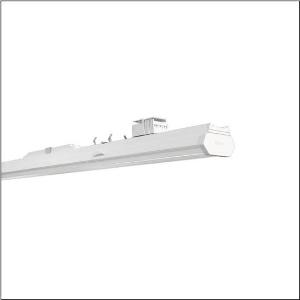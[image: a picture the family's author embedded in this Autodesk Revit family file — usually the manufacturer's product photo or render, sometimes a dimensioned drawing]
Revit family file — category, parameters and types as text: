
# Revit family: licross_r__11_protected_ho_51tp12dn4fxm3s4_aaf8
name_source: partatom
category: Lighting Fixtures
units: mm (PartAtom-declared; Revit-internal decimal feet)

## family parameters
Cut with Voids When Loaded = No
Host = Face
Light Source = No
Part Type = Normal
Room Calculation Point = No
Round Connector Dimension = Use Diameter
Shared = No

## types (1)
- --- (1 x LED, 970 lm, 7.4 W, 4000K)
    Apparent Load = 7 VA
    CIE Flux Codes = 70 91 97 98 100
    Color Rendering = 80
    Color Temperature = 4000K
    Default Elevation = 1800 mm
    Description = Licross® 11 Protected HO, luminaire insert, of sheet steel, galvanised, coil coated, white, length: 1.500mm, width: 90mm, height: 101mm, LED rated luminous flux: 15.270lm, light colour: 840, control gear: DALI 2, with plug, 6-pole, with phase selection, for trunking rail, 9 or 11-core, mains connection: 220..240V, AC, 50/60Hz, rated input power: 91W, for trunking rail, 9-/11-core, halogen-free wiring, for emergency light function, converter,control gear: single battery element, battery: LiFePO4, 9Ah, primary light control with lens, of plastic, primary optical cover: cover, of PMMA, light emission: direct distribution, primary light characteristic: symmetric, protection rating (complete): IP64, insulation class (complete): insulation class I (protective earthing), certification: CE, UKCA, protection symbol: D if used in an environment with conductive dust loads with corresponding accessories, impact resistance: IK06, permissible ambient temperature for indoor applications: +5..+30°C, standard: EN 60598-2-22, LABS conformity tested according to VDMA 24364:2018-05, reducing of maximum allowable ambient temperature of 5°C with ceiling mounting, corresponds to IFS (International Featured Standards) requirements for safety and quality in the food industry, packaging unit: 1 piece
    Height = 92 mm
    Lamp = 1 x LED
    Lamp Light Flux = 970 lm
    Lamp Power = 7.4 W
    Lamp count = 1
    Length = 1500 mm
    Luminous efficacy = 131 lm/W
    Manufacturer = Siteco
    ModVariant = No
    Model = 51TP12DN4FXM3S4
    Mounting Place = Ceiling
    Mounting Type = Pendant
    Number of Poles = 1
    OnlyDefault = Yes
    Power Factor = 1
    Product Name = Licross® 11 Protected HO
    Product group = luminaire insert
    ProductGroupID = 901
    Protection Class = Protection class I
    Protection Degree = IP 64
    RLX_Detail_Level = 1
    RLX_Emergency_Light_Flux = 0 lm
    RLX_Emergency_Type = 0
    RLX_Emergency_Type_DB = No
    RlxData = <blob elided: 24793 chars, md5=59a09943>
    Socket = socket
    Standby Power = 0 W
    System Light Flux = 970 lm
    System Power = 7 W
    Type Comments = : emergency light operation: 3 h
    Type Image = l_1256148.jpg
    URL = http://relux.com
    VarID = @adj_059619
    Voltage = 0 V
    Weight = 0.00 kg
    Width = 88 mm

## geometry (parser evidence)
native form markers: Blend x4, Sweep x11
no freeform markers — native parametric forms only
